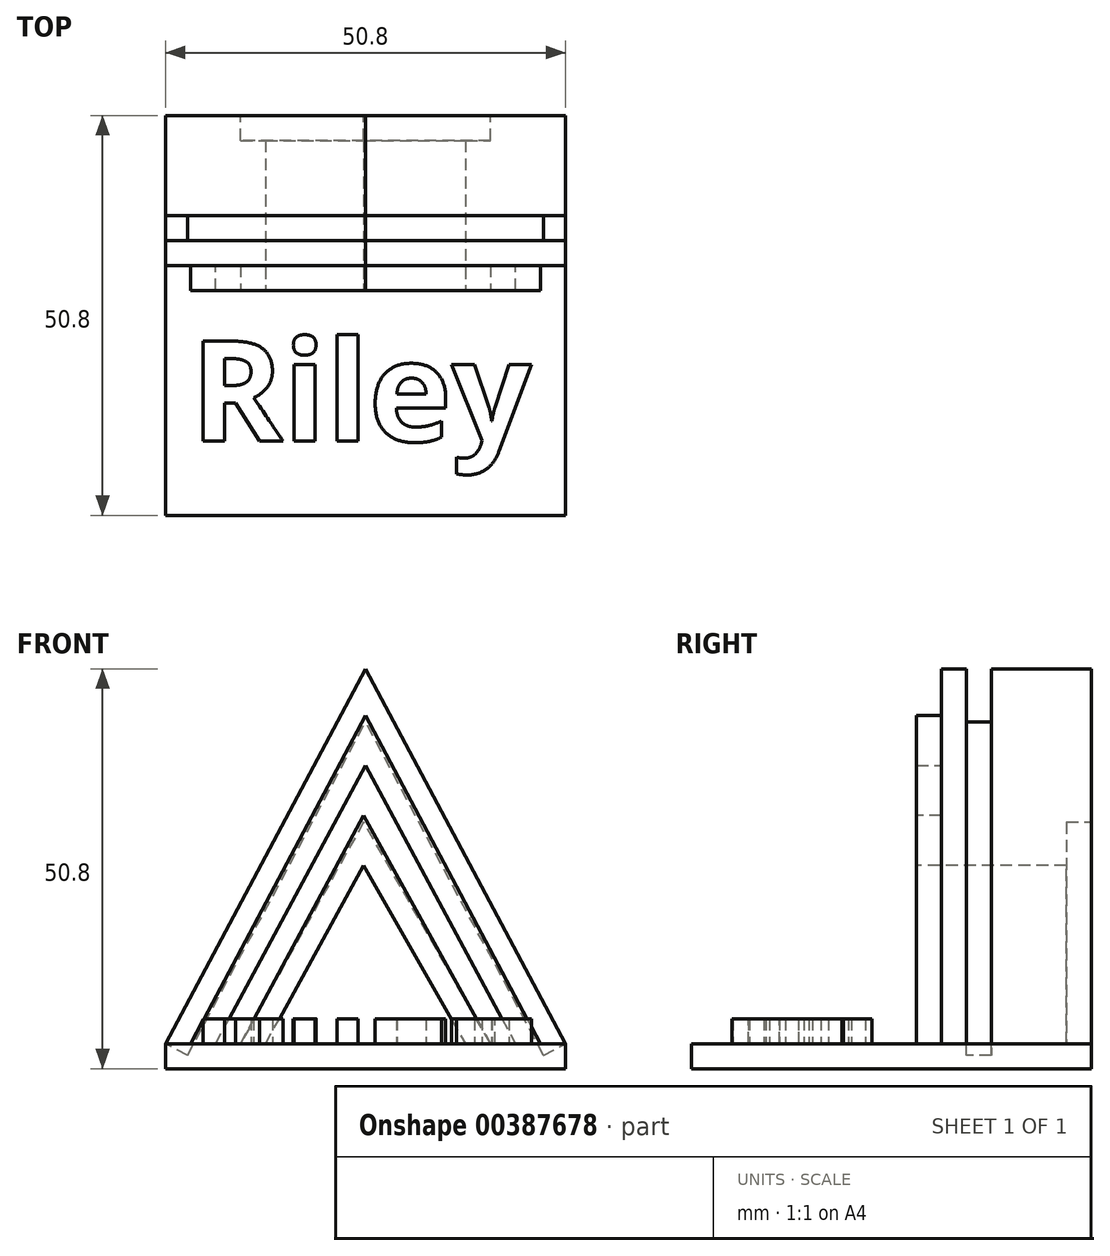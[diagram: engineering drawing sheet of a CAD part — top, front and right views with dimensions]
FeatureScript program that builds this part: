
annotation { "Feature Type Name" : "Feature", "Feature Type Description" : "" }
export const myFeature = defineFeature(function(context is Context, id is Id, definition is map)
    precondition{}
    {
        {
            var Q0;
            Q0=qCreatedBy(makeId("Front.planeOp"),FACE);
            var sketch = newSketch(context, id + "F0", { "sketchPlane" : qUnion([Q0])});
            skLineSegment(sketch, "E0", {"start": v(0, 0) * mm, "end": v(50.8, 0) * mm});
            skLineSegment(sketch, "E1", {"start": v(50.8, 0) * mm, "end": v(50.8, 50.8) * mm});
            skLineSegment(sketch, "E2", {"start": v(50.8, 50.8) * mm, "end": v(0, 50.8) * mm});
            skLineSegment(sketch, "E3", {"start": v(0, 50.8) * mm, "end": v(0, 0) * mm});
            skSolve(sketch);
        }
        {
            var Q0;
            Q0=makeQuery(id+"F0.imprint","IMPRINT",FACE,{"disambiguationData":[TD([[makeQuery(id+"F0.imprint","IMPRINT",EDGE,{"derivedFrom":sQuery(id+"F0.wireOp",EDGE,"E0")}),1.0]])]});
            extrude(context, id + "F1", {"entities" : qUnion([Q0]), "depth" : 50.8 * mm});
        }
        {
            var Q0;
            Q0=makeQuery(id+"F1.opExtrude","CAP_FACE",FACE,{"disambiguationData":[OSD([sQuery(id+"F0.wireOp",EDGE,"E0"),sQuery(id+"F0.wireOp",EDGE,"E1"),sQuery(id+"F0.wireOp",EDGE,"E2"),sQuery(id+"F0.wireOp",EDGE,"E3")])],"isStart":false});
            var sketch = newSketch(context, id + "F2", { "sketchPlane" : qUnion([Q0])});
            skLineSegment(sketch, "E4", {"start": v(0, 3.17) * mm, "end": v(50.8, 3.18) * mm});
            skLineSegment(sketch, "E5", {"start": v(0, 3.17) * mm, "end": v(0, 0) * mm});
            skLineSegment(sketch, "E6", {"start": v(0, 0) * mm, "end": v(50.8, 0) * mm});
            skLineSegment(sketch, "E7", {"start": v(50.8, 0) * mm, "end": v(50.8, 3.18) * mm});
            skSolve(sketch);
        }
        {
            var Q0;
            {var subQ0=sQuery(id+"F2.wireOp",EDGE,"E4");Q0=makeQuery(id+"F2.imprint","IMPRINT",FACE,{"disambiguationData":[TD([[makeQuery(id+"F2.imprint","IMPRINT",EDGE,{"derivedFrom":subQ0}),1.0]])]});}
            extrude(context, id + "F3", {"entities" : qUnion([Q0]), "operationType" : NewBodyOperationType.REMOVE, "oppositeDirection" : true, "depth" : 31.75 * mm});
        }
        {
            var Q0;
            Q0=makeQuery(id+"F3.boolean.opBoolean","COPY",FACE,{"derivedFrom":makeQuery(id+"F3.opExtrude","CAP_FACE",FACE,{"disambiguationData":[OSD([sQuery(id+"F0.wireOp",EDGE,"E1"),sQuery(id+"F0.wireOp",EDGE,"E2"),sQuery(id+"F0.wireOp",EDGE,"E3"),sQuery(id+"F2.wireOp",EDGE,"E4")])],"isStart":false})});
            var sketch = newSketch(context, id + "F4", { "sketchPlane" : qUnion([Q0])});
            skLineSegment(sketch, "E8", {"start": v(0, 3.18) * mm, "end": v(25.4, 50.8) * mm});
            skLineSegment(sketch, "E9", {"start": v(25.4, 50.8) * mm, "end": v(50.8, 3.18) * mm});
            skLineSegment(sketch, "E10", {"start": v(50.8, 3.18) * mm, "end": v(0, 3.18) * mm});
            skSolve(sketch);
        }
        {
            var Q0;
            {var subQ0=sQuery(id+"F4.wireOp",EDGE,"E8");Q0=makeQuery(id+"F4.imprint","IMPRINT",FACE,{"disambiguationData":[TD([[makeQuery(id+"F4.imprint","IMPRINT",EDGE,{"derivedFrom":subQ0}),1.0]])]});}
            var Q1;
            {var subQ0=sQuery(id+"F4.wireOp",EDGE,"E9");Q1=makeQuery(id+"F4.imprint","IMPRINT",FACE,{"disambiguationData":[TD([[makeQuery(id+"F4.imprint","IMPRINT",EDGE,{"derivedFrom":subQ0}),1.0]])]});}
            extrude(context, id + "F5", {"entities" : qUnion([Q0, Q1]), "operationType" : NewBodyOperationType.REMOVE, "oppositeDirection" : true, "depth" : 19.05 * mm});
        }
        {
            var Q0;
            Q0=makeQuery(id+"F3.boolean.opBoolean","COPY",FACE,{"derivedFrom":makeQuery(id+"F3.opExtrude","CAP_FACE",FACE,{"disambiguationData":[OSD([sQuery(id+"F0.wireOp",EDGE,"E1"),sQuery(id+"F0.wireOp",EDGE,"E2"),sQuery(id+"F0.wireOp",EDGE,"E3"),sQuery(id+"F2.wireOp",EDGE,"E4")])],"isStart":false})});
            var sketch = newSketch(context, id + "F6", { "sketchPlane" : qUnion([Q0])});
            skLineSegment(sketch, "E11", {"start": v(3.17, 3.17) * mm, "end": v(25.4, 44.85) * mm});
            skLineSegment(sketch, "E12", {"start": v(25.4, 44.85) * mm, "end": v(47.63, 3.18) * mm});
            skLineSegment(sketch, "E13", {"start": v(47.63, 3.18) * mm, "end": v(3.18, 3.17) * mm});
            skSolve(sketch);
        }
        {
            var Q0;
            Q0=makeQuery(id+"F6.imprint","IMPRINT",FACE,{"disambiguationData":[TD([[makeQuery(id+"F6.imprint","IMPRINT",EDGE,{"derivedFrom":sQuery(id+"F6.wireOp",EDGE,"E11")}),-1.0]])]});
            var sketch = newSketch(context, id + "F7", { "sketchPlane" : qUnion([Q0])});
            skLineSegment(sketch, "E14", {"start": v(6.35, 3.17) * mm, "end": v(25.4, 38.5) * mm});
            skLineSegment(sketch, "E15", {"start": v(25.4, 38.5) * mm, "end": v(44.45, 3.17) * mm});
            skLineSegment(sketch, "E16", {"start": v(44.45, 3.17) * mm, "end": v(6.35, 3.18) * mm});
            skSolve(sketch);
        }
        {
            var Q0;
            {var subQ3=sQuery(id+"F7.wireOp",EDGE,"E14");Q0=makeQuery(id+"F7.imprint","IMPRINT",FACE,{"disambiguationData":[TD([[makeQuery(id+"F7.imprint","IMPRINT",EDGE,{"derivedFrom":subQ3}),1.0]])]});}
            extrude(context, id + "F8", {"entities" : qUnion([Q0]), "operationType" : NewBodyOperationType.ADD, "depth" : 3.17 * mm});
        }
        {
            var Q0;
            Q0=makeQuery(id+"F8.opExtrude","CAP_FACE",FACE,{"disambiguationData":[OSD([sQuery(id+"F6.wireOp",EDGE,"E11"),sQuery(id+"F6.wireOp",EDGE,"E12"),sQuery(id+"F6.wireOp",EDGE,"E13"),sQuery(id+"F7.wireOp",EDGE,"E14"),sQuery(id+"F7.wireOp",EDGE,"E15")])],"isStart":false});
            var sketch = newSketch(context, id + "F9", { "sketchPlane" : qUnion([Q0])});
            skLineSegment(sketch, "E17", {"start": v(9.52, 3.17) * mm, "end": v(25.15, 32.15) * mm});
            skLineSegment(sketch, "E18", {"start": v(25.15, 32.15) * mm, "end": v(41.28, 3.17) * mm});
            skLineSegment(sketch, "E19", {"start": v(41.28, 3.18) * mm, "end": v(9.52, 3.17) * mm});
            skSolve(sketch);
        }
        {
            var Q0;
            Q0=makeQuery(id+"F9.imprint","IMPRINT",FACE,{"disambiguationData":[TD([[makeQuery(id+"F9.imprint","IMPRINT",EDGE,{"derivedFrom":sQuery(id+"F9.wireOp",EDGE,"E17")}),-1.0]])]});
            extrude(context, id + "F10", {"entities" : qUnion([Q0]), "operationType" : NewBodyOperationType.ADD, "oppositeDirection" : true, "depth" : 3.17 * mm});
        }
        {
            var Q0;
            Q0=makeQuery(id+"F10.opExtrude","CAP_FACE",FACE,{"disambiguationData":[OSD([sQuery(id+"F9.wireOp",EDGE,"E17"),sQuery(id+"F9.wireOp",EDGE,"E18"),sQuery(id+"F9.wireOp",EDGE,"E19")])],"isStart":true});
            var sketch = newSketch(context, id + "F11", { "sketchPlane" : qUnion([Q0])});
            skLineSegment(sketch, "E20", {"start": v(12.7, 3.17) * mm, "end": v(25.15, 25.8) * mm});
            skLineSegment(sketch, "E21", {"start": v(25.15, 25.8) * mm, "end": v(38.1, 3.17) * mm});
            skLineSegment(sketch, "E22", {"start": v(38.1, 3.18) * mm, "end": v(12.7, 3.17) * mm});
            skSolve(sketch);
        }
        {
            var Q0;
            Q0=makeQuery(id+"F11.imprint","IMPRINT",FACE,{"disambiguationData":[TD([[makeQuery(id+"F11.imprint","IMPRINT",EDGE,{"derivedFrom":sQuery(id+"F11.wireOp",EDGE,"E20")}),-1.0]])]});
            extrude(context, id + "F12", {"entities" : qUnion([Q0]), "operationType" : NewBodyOperationType.REMOVE, "oppositeDirection" : true, "depth" : 22.22 * mm});
        }
        {
            var Q0;
            Q0=makeQuery(id+"F5.boolean.opBoolean","COPY",FACE,{"derivedFrom":makeQuery(id+"F5.opExtrude","SWEPT_FACE",FACE,{"disambiguationData":[OSD([sQuery(id+"F4.wireOp",EDGE,"E8")])]})});
            var sketch = newSketch(context, id + "F13", { "sketchPlane" : qUnion([Q0])});
            skLineSegment(sketch, "E23", {"start": v(12.7, 56.78) * mm, "end": v(12.7, 2.8) * mm});
            skLineSegment(sketch, "E24", {"start": v(12.7, 2.8) * mm, "end": v(15.88, 2.8) * mm});
            skLineSegment(sketch, "E25", {"start": v(15.88, 2.8) * mm, "end": v(15.88, 56.78) * mm});
            skLineSegment(sketch, "E26", {"start": v(15.88, 56.78) * mm, "end": v(12.7, 56.78) * mm});
            skSolve(sketch);
        }
        {
            var Q0;
            Q0=makeQuery(id+"F13.imprint","IMPRINT",FACE,{"disambiguationData":[TD([[makeQuery(id+"F13.imprint","IMPRINT",EDGE,{"derivedFrom":sQuery(id+"F13.wireOp",EDGE,"E23")}),1.0]])]});
            extrude(context, id + "F14", {"entities" : qUnion([Q0]), "operationType" : NewBodyOperationType.REMOVE, "oppositeDirection" : true, "depth" : 3.17 * mm});
        }
        {
            var Q0;
            Q0=makeQuery(id+"F5.boolean.opBoolean","COPY",FACE,{"derivedFrom":makeQuery(id+"F5.opExtrude","SWEPT_FACE",FACE,{"disambiguationData":[OSD([sQuery(id+"F4.wireOp",EDGE,"E9")])]})});
            var sketch = newSketch(context, id + "F15", { "sketchPlane" : qUnion([Q0])});
            skLineSegment(sketch, "E27", {"start": v(-15.88, 29.05) * mm, "end": v(-15.88, -21.1) * mm});
            skLineSegment(sketch, "E28", {"start": v(-15.88, -21.1) * mm, "end": v(-12.7, -21.1) * mm});
            skLineSegment(sketch, "E29", {"start": v(-12.7, -21.1) * mm, "end": v(-12.7, 29.05) * mm});
            skLineSegment(sketch, "E30", {"start": v(-12.7, 29.05) * mm, "end": v(-15.88, 29.05) * mm});
            skSolve(sketch);
        }
        {
            var Q0;
            Q0 = qSketchRegion(id + "F15", true);
            extrude(context, id + "F16", {"entities" : qUnion([Q0]), "operationType" : NewBodyOperationType.REMOVE, "oppositeDirection" : true, "depth" : 3.17 * mm});
        }
        {
            var Q0;
            Q0=makeQuery(id+"F1.opExtrude","CAP_FACE",FACE,{"disambiguationData":[OSD([sQuery(id+"F0.wireOp",EDGE,"E0"),sQuery(id+"F0.wireOp",EDGE,"E1"),sQuery(id+"F0.wireOp",EDGE,"E2"),sQuery(id+"F0.wireOp",EDGE,"E3")])],"isStart":true});
            var sketch = newSketch(context, id + "F17", { "sketchPlane" : qUnion([Q0])});
            skLineSegment(sketch, "E31", {"start": v(-41.28, 3.18) * mm, "end": v(-25.15, 31.35) * mm});
            skLineSegment(sketch, "E32", {"start": v(-25.15, 31.35) * mm, "end": v(-9.53, 3.18) * mm});
            skLineSegment(sketch, "E33", {"start": v(-9.52, 3.18) * mm, "end": v(-41.28, 3.17) * mm});
            skSolve(sketch);
        }
        {
            var Q0;
            {var subQ2=sQuery(id+"F17.wireOp",EDGE,"E31");Q0=makeQuery(id+"F17.imprint","IMPRINT",FACE,{"disambiguationData":[TD([[makeQuery(id+"F17.imprint","IMPRINT",EDGE,{"derivedFrom":subQ2}),-1.0]])]});}
            extrude(context, id + "F18", {"entities" : qUnion([Q0]), "operationType" : NewBodyOperationType.REMOVE, "oppositeDirection" : true, "depth" : 3.17 * mm});
        }
        {
            var Q0;
            {var subQ0=sQuery(id+"F17.wireOp",EDGE,"E33");Q0=makeQuery(id+"F18.boolean.opBoolean","MERGE",FACE,{"derivedFrom":[makeQuery(id+"F12.boolean.opBoolean","MERGE",FACE,{"derivedFrom":[makeQuery(id+"F3.boolean.opBoolean","COPY",FACE,{"derivedFrom":makeQuery(id+"F3.opExtrude","SWEPT_FACE",FACE,{"disambiguationData":[OSD([sQuery(id+"F2.wireOp",EDGE,"E4")])]})}),makeQuery(id+"F12.opExtrude","SWEPT_FACE",FACE,{"disambiguationData":[OSD([sQuery(id+"F11.wireOp",EDGE,"E22")])]})]}),makeQuery(id+"F18.opExtrude","SWEPT_FACE",FACE,{"disambiguationData":[OSD([subQ0]),TDD([makeQuery(id+"F17.imprint","IMPRINT",EDGE,{"disambiguationData":[TD([[makeQuery(id+"F17.imprint","INTERSECT",VERTEX,{"derivedFrom":[makeQuery(id+"F12.boolean.opBoolean","COPY",EDGE,{"derivedFrom":makeQuery(id+"F12.opExtrude","CAP_EDGE",EDGE,{"disambiguationData":[OSD([sQuery(id+"F11.wireOp",EDGE,"E20")])],"isStart":false})}),subQ0]}),1.0],[makeQuery(id+"F17.imprint","INTERSECT",VERTEX,{"derivedFrom":[sQuery(id+"F17.wireOp",EDGE,"E32"),subQ0]}),-1.0]])],"derivedFrom":subQ0})])]}),makeQuery(id+"F18.opExtrude","SWEPT_FACE",FACE,{"disambiguationData":[OSD([subQ0]),TDD([makeQuery(id+"F17.imprint","IMPRINT",EDGE,{"disambiguationData":[TD([[makeQuery(id+"F17.imprint","INTERSECT",VERTEX,{"derivedFrom":[makeQuery(id+"F12.boolean.opBoolean","COPY",EDGE,{"derivedFrom":makeQuery(id+"F12.opExtrude","CAP_EDGE",EDGE,{"disambiguationData":[OSD([sQuery(id+"F11.wireOp",EDGE,"E21")])],"isStart":false})}),subQ0]}),-1.0],[makeQuery(id+"F17.imprint","INTERSECT",VERTEX,{"derivedFrom":[sQuery(id+"F17.wireOp",EDGE,"E31"),subQ0]}),1.0]])],"derivedFrom":subQ0})])]})]});}
            var sketch = newSketch(context, id + "F19", { "sketchPlane" : qUnion([Q0])});
            skText(sketch, "E34", { "text": "Riley", "fontName": "OpenSans-Bold.ttf"});
            const initialGuessF19  = {"E34": [0.00318, -0.0414, 1, 0, 0.01283]};
            skSetInitialGuess(sketch, initialGuessF19);
            skSolve(sketch);
        }
        {
            var Q0;
            Q0=makeQuery(id+"F19.imprint","IMPRINT",FACE,{"disambiguationData":[TD([[makeQuery(id+"F19.imprint","IMPRINT",EDGE,{"derivedFrom":sQuery(id+"F19.wireOp",EDGE,"E34.sketch_text.stroke-0")}),-1.0]])]});
            var Q1;
            Q1=makeQuery(id+"F19.imprint","IMPRINT",FACE,{"disambiguationData":[TD([[makeQuery(id+"F19.imprint","IMPRINT",EDGE,{"derivedFrom":sQuery(id+"F19.wireOp",EDGE,"E34.sketch_text.stroke-24")}),-1.0]])]});
            var Q2;
            Q2=makeQuery(id+"F19.imprint","IMPRINT",FACE,{"disambiguationData":[TD([[makeQuery(id+"F19.imprint","IMPRINT",EDGE,{"derivedFrom":sQuery(id+"F19.wireOp",EDGE,"E34.sketch_text.stroke-19")}),-1.0]])]});
            var Q3;
            Q3=makeQuery(id+"F19.imprint","IMPRINT",FACE,{"disambiguationData":[TD([[makeQuery(id+"F19.imprint","IMPRINT",EDGE,{"derivedFrom":sQuery(id+"F19.wireOp",EDGE,"E34.sketch_text.stroke-28")}),-1.0]])]});
            var Q4;
            Q4=makeQuery(id+"F19.imprint","IMPRINT",FACE,{"disambiguationData":[TD([[makeQuery(id+"F19.imprint","IMPRINT",EDGE,{"derivedFrom":sQuery(id+"F19.wireOp",EDGE,"E34.sketch_text.stroke-32")}),-1.0]])]});
            var Q5;
            Q5=makeQuery(id+"F19.imprint","IMPRINT",FACE,{"disambiguationData":[TD([[makeQuery(id+"F19.imprint","IMPRINT",EDGE,{"derivedFrom":sQuery(id+"F19.wireOp",EDGE,"E34.sketch_text.stroke-52")}),-1.0]])]});
            extrude(context, id + "F20", {"entities" : qUnion([Q0, Q1, Q2, Q3, Q4, Q5]), "operationType" : NewBodyOperationType.ADD, "depth" : 3.17 * mm});
        }
    });
